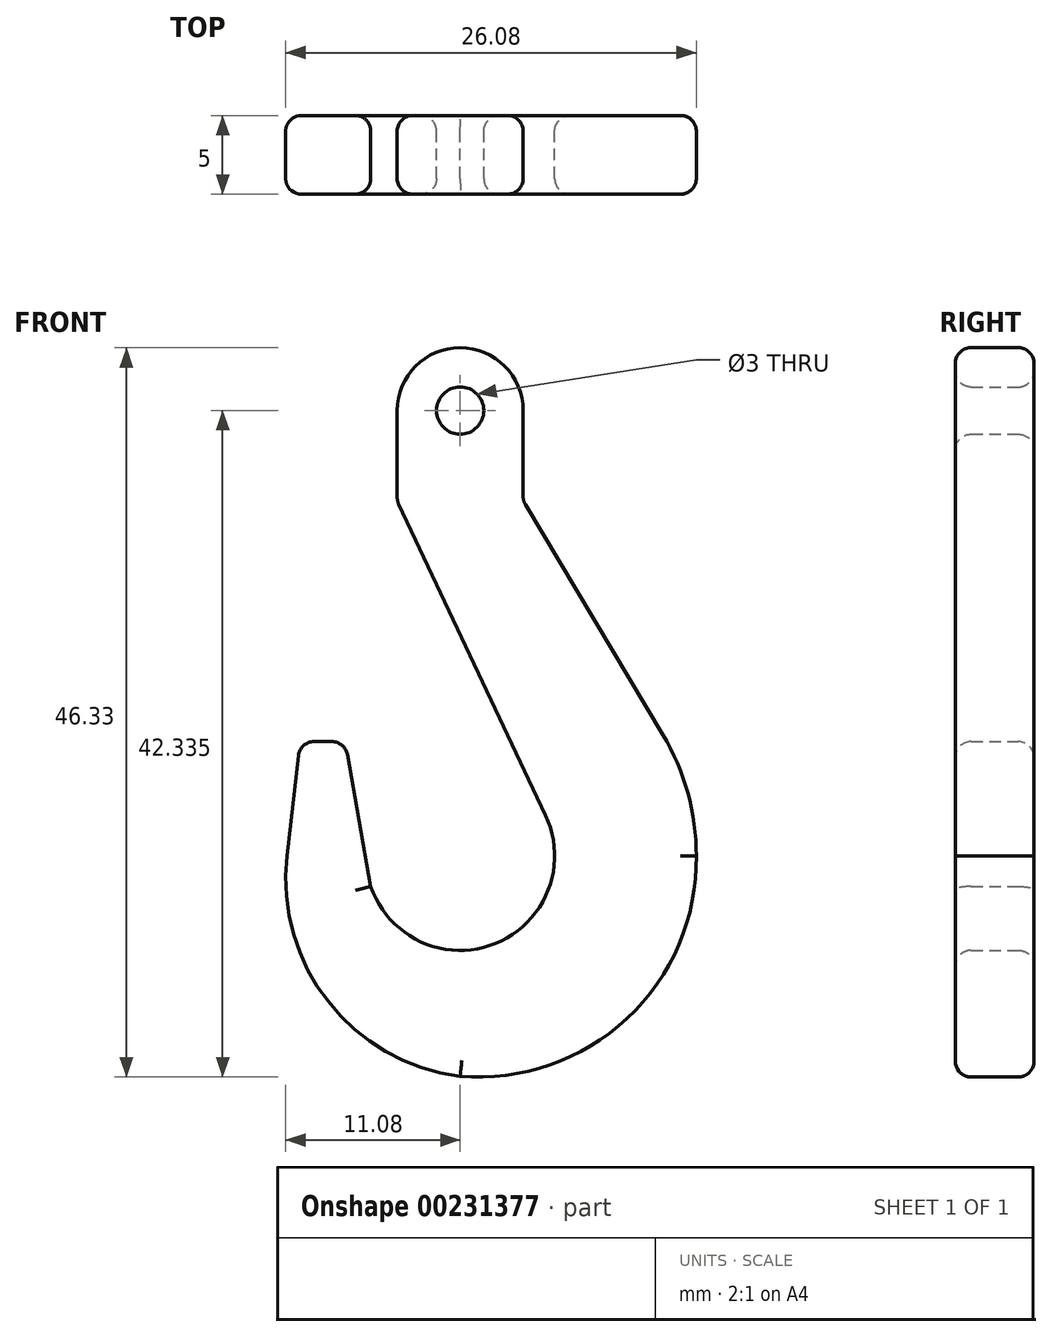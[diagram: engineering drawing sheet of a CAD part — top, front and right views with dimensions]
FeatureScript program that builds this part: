
annotation { "Feature Type Name" : "Feature", "Feature Type Description" : "" }
export const myFeature = defineFeature(function(context is Context, id is Id, definition is map)
    precondition{}
    {
        {
            var Q0;
            Q0=qCreatedBy(makeId("Front.planeOp"),FACE);
            var sketch = newSketch(context, id + "F0", { "sketchPlane" : qUnion([Q0])});
            skCircle(sketch, "E0", {"center": v(0, 28.28) * mm, "radius": 4 * mm});
            skLineSegment(sketch, "E1", {"start": v(0, 0) * mm, "end": v(0, 51.13) * mm, "construction": true});
            skLineSegment(sketch, "E2.0", {"start": v(4, 0) * mm, "end": v(4, 16.6) * mm, "construction": true});
            skLineSegment(sketch, "E3.0", {"start": v(-4, 0) * mm, "end": v(-4, 28.28) * mm, "construction": true});
            skLineSegment(sketch, "E4", {"start": v(4, 38.9) * mm, "end": v(4, 22.55) * mm});
            skLineSegment(sketch, "E5", {"start": v(-4, 38.35) * mm, "end": v(-4, 18) * mm});
            skLineSegment(sketch, "E6.trimOffspring", {"start": v(-4, 38.35) * mm, "end": v(-4, 51.13) * mm, "construction": true});
            skLineSegment(sketch, "E7.trimOffspring", {"start": v(4, 38.9) * mm, "end": v(4, 51.13) * mm, "construction": true});
            skLineSegment(sketch, "E8", {"start": v(4, 22.55) * mm, "end": v(12.88, 7.7) * mm});
            skLineSegment(sketch, "E9.trimOffspring", {"start": v(4, 22.55) * mm, "end": v(4, 28.28) * mm, "construction": true});
            skLineSegment(sketch, "E10", {"start": v(-4, 28.28) * mm, "end": v(-4, 22.55) * mm});
            skPoint(sketch, "E11.orphan", {"position": v(-8.14, 16.4) * mm});
            skCircle(sketch, "E12", {"center": v(0, 28.28) * mm, "radius": 1.5 * mm});
            skPoint(sketch, "E13.start.orphan", {"position": v(-8.14, 0) * mm});
            skPoint(sketch, "E14.orphan", {"position": v(-8.14, 13.67) * mm});
            skLineSegment(sketch, "E15", {"start": v(-4, 22.55) * mm, "end": v(5.43, 2.56) * mm});
            skCircle(sketch, "E16.0", {"center": v(0, 0) * mm, "radius": 14 * mm, "construction": true});
            skCircle(sketch, "E17.0", {"center": v(0, 0) * mm, "radius": 11 * mm, "construction": true});
            skLineSegment(sketch, "E18", {"start": v(0, 0) * mm, "end": v(-32.75, 0) * mm, "construction": true});
            skLineSegment(sketch, "E19", {"start": v(0, 0) * mm, "end": v(0, -17.8) * mm, "construction": true});
            skArc(sketch, "E20", {"start": v(-11, 0) * mm, "mid": v(-8.38, -9.26) * mm, "end": v(0, -14) * mm});
            skArc(sketch, "E21", {"start": v(0, -14) * mm, "mid": v(10.6, -10.32) * mm, "end": v(15, 0) * mm});
            skPoint(sketch, "E22.start.orphan", {"position": v(7.1, 3.98) * mm});
            skLineSegment(sketch, "E23", {"start": v(-7.31, 7.26) * mm, "end": v(-10.17, 7.26) * mm});
            skLineSegment(sketch, "E24", {"start": v(-11, 0) * mm, "end": v(-10.17, 7.26) * mm});
            skPoint(sketch, "E25.start.orphan", {"position": v(-11, 7.26) * mm});
            skLineSegment(sketch, "E26", {"start": v(-5.68, -1.94) * mm, "end": v(-7.31, 7.26) * mm});
            skArc(sketch, "E27.trimOffspring", {"start": v(-5.68, -1.94) * mm, "mid": v(2.25, -5.56) * mm, "end": v(5.43, 2.56) * mm});
            skArc(sketch, "E28", {"start": v(15, 0) * mm, "mid": v(14.46, 4) * mm, "end": v(12.88, 7.7) * mm});
            skSolve(sketch);
        }
        {
            var Q0;
            {var subQ4=sQuery(id+"F0.wireOp",EDGE,"E8");Q0=makeQuery(id+"F0.imprint","IMPRINT",FACE,{"disambiguationData":[TD([[makeQuery(id+"F0.imprint","IMPRINT",EDGE,{"derivedFrom":subQ4}),-1.0]])]});}
            var Q1;
            Q1=makeQuery(id+"F0.imprint","IMPRINT",FACE,{"disambiguationData":[TD([[makeQuery(id+"F0.imprint","IMPRINT",EDGE,{"derivedFrom":sQuery(id+"F0.wireOp",EDGE,"E12")}),-1.0]])]});
            extrude(context, id + "F1", {"entities" : qUnion([Q0, Q1]), "endBound" : BoundingType.SYMMETRIC, "depth" : 5 * mm});
        }
        {
            var Q0;
            Q0=makeQuery(id+"F1.opExtrude","SWEPT_EDGE",EDGE,{"disambiguationData":[OSD([sQuery(id+"F0.wireOp",EDGE,"E23"),sQuery(id+"F0.wireOp",EDGE,"E24")])]});
            var Q1;
            Q1=makeQuery(id+"F1.opExtrude","SWEPT_EDGE",EDGE,{"disambiguationData":[OSD([sQuery(id+"F0.wireOp",EDGE,"E23"),sQuery(id+"F0.wireOp",EDGE,"E26")])]});
            var Q2;
            Q2=makeQuery(id+"F1.opExtrude","SWEPT_EDGE",EDGE,{"disambiguationData":[OSD([sQuery(id+"F0.wireOp",EDGE,"E4"),sQuery(id+"F0.wireOp",EDGE,"E8")])]});
            var Q3;
            Q3=makeQuery(id+"F1.opExtrude","SWEPT_EDGE",EDGE,{"disambiguationData":[OSD([sQuery(id+"F0.wireOp",EDGE,"E10"),sQuery(id+"F0.wireOp",EDGE,"E15")])]});
            fillet(context, id + "F2", {"entities" : qUnion([Q0, Q1, Q2, Q3]), "radius" : 1 * mm, "tangentPropagation" : true, "allowEdgeOverflow" : false});
        }
        {
            var Q0;
            Q0=makeQuery(id+"F1.opExtrude","CAP_FACE",FACE,{"disambiguationData":[OSD([sQuery(id+"F0.wireOp",EDGE,"E0"),sQuery(id+"F0.wireOp",EDGE,"E4"),sQuery(id+"F0.wireOp",EDGE,"E8"),sQuery(id+"F0.wireOp",EDGE,"E10"),sQuery(id+"F0.wireOp",EDGE,"E12"),sQuery(id+"F0.wireOp",EDGE,"E15"),sQuery(id+"F0.wireOp",EDGE,"E20"),sQuery(id+"F0.wireOp",EDGE,"E21"),sQuery(id+"F0.wireOp",EDGE,"E23"),sQuery(id+"F0.wireOp",EDGE,"E24"),sQuery(id+"F0.wireOp",EDGE,"E26"),sQuery(id+"F0.wireOp",EDGE,"E27.trimOffspring"),sQuery(id+"F0.wireOp",EDGE,"E28")])],"isStart":true});
            var Q1;
            Q1=makeQuery(id+"F1.opExtrude","CAP_FACE",FACE,{"disambiguationData":[OSD([sQuery(id+"F0.wireOp",EDGE,"E0"),sQuery(id+"F0.wireOp",EDGE,"E4"),sQuery(id+"F0.wireOp",EDGE,"E8"),sQuery(id+"F0.wireOp",EDGE,"E10"),sQuery(id+"F0.wireOp",EDGE,"E12"),sQuery(id+"F0.wireOp",EDGE,"E15"),sQuery(id+"F0.wireOp",EDGE,"E20"),sQuery(id+"F0.wireOp",EDGE,"E21"),sQuery(id+"F0.wireOp",EDGE,"E23"),sQuery(id+"F0.wireOp",EDGE,"E24"),sQuery(id+"F0.wireOp",EDGE,"E26"),sQuery(id+"F0.wireOp",EDGE,"E27.trimOffspring"),sQuery(id+"F0.wireOp",EDGE,"E28")])],"isStart":false});
            fillet(context, id + "F3", {"entities" : qUnion([Q0, Q1]), "radius" : 1 * mm, "tangentPropagation" : true, "allowEdgeOverflow" : false});
        }
    });
